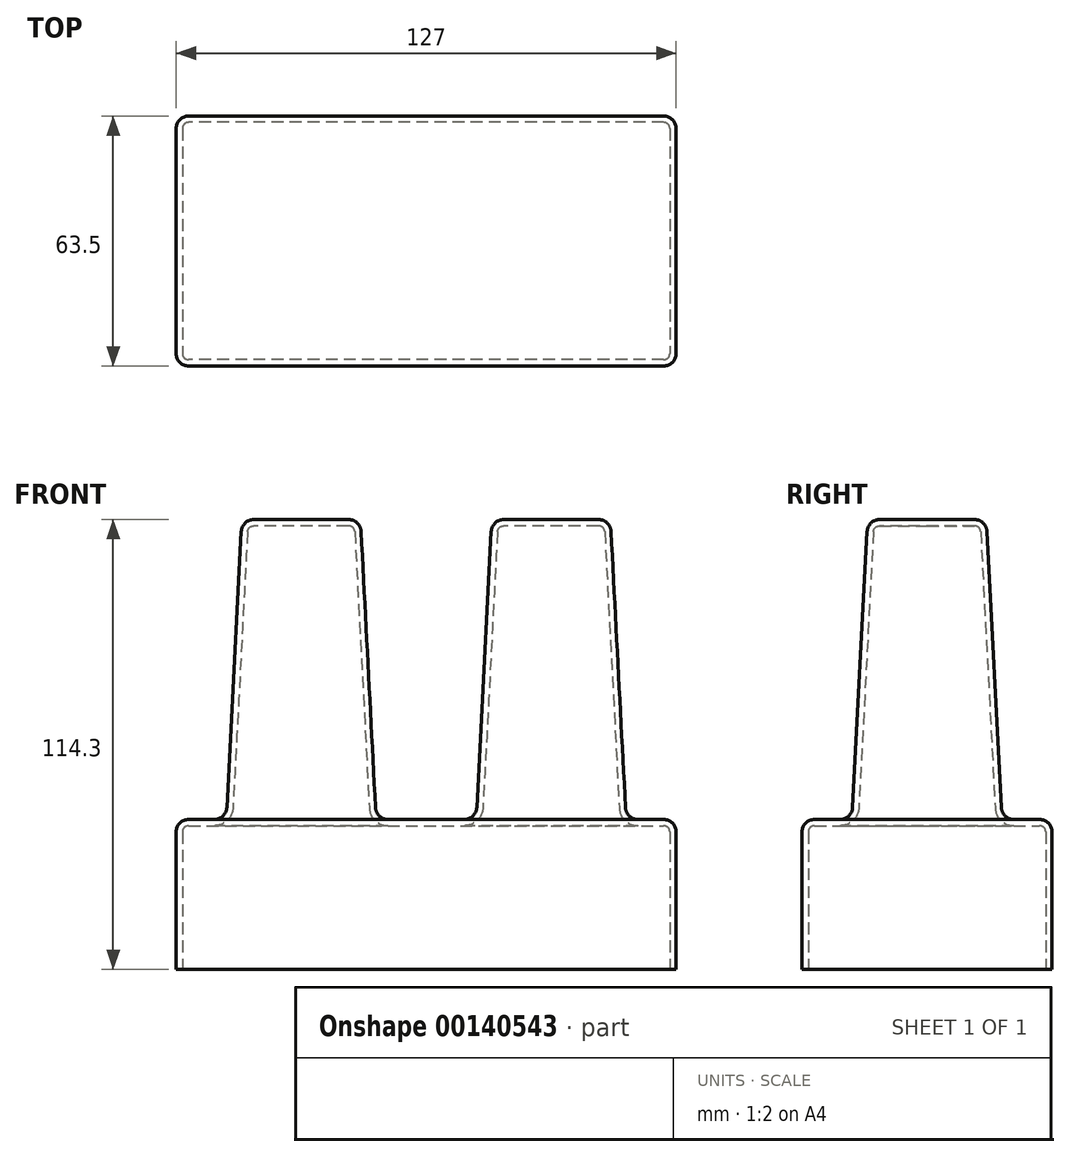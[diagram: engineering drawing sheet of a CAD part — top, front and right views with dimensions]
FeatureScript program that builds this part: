
annotation { "Feature Type Name" : "Feature", "Feature Type Description" : "" }
export const myFeature = defineFeature(function(context is Context, id is Id, definition is map)
    precondition{}
    {
        {
            var Q0;
            Q0=qCreatedBy(makeId("Top.planeOp"),FACE);
            var sketch = newSketch(context, id + "F0", { "sketchPlane" : qUnion([Q0])});
            skLineSegment(sketch, "E0.bottom", {"start": v(63.5, 31.75) * mm, "end": v(-63.5, 31.75) * mm});
            skLineSegment(sketch, "E0.top", {"start": v(63.5, -31.75) * mm, "end": v(-63.5, -31.75) * mm});
            skLineSegment(sketch, "E0.left", {"start": v(63.5, 31.75) * mm, "end": v(63.5, -31.75) * mm});
            skLineSegment(sketch, "E0.right", {"start": v(-63.5, 31.75) * mm, "end": v(-63.5, -31.75) * mm});
            skPoint(sketch, "E0.middle", {"position": v(0, 0) * mm});
            skSolve(sketch);
        }
        {
            var Q0;
            Q0 = qSketchRegion(id + "F0", true);
            extrude(context, id + "F1", {"entities" : qUnion([Q0]), "depth" : 38.1 * mm});
        }
        {
            var Q0;
            Q0=makeQuery(id+"F1.opExtrude","CAP_FACE",FACE,{"disambiguationData":[OSD([sQuery(id+"F0.wireOp",EDGE,"E0.bottom"),sQuery(id+"F0.wireOp",EDGE,"E0.top"),sQuery(id+"F0.wireOp",EDGE,"E0.left"),sQuery(id+"F0.wireOp",EDGE,"E0.right")])],"isStart":false});
            var sketch = newSketch(context, id + "F5", { "sketchPlane" : qUnion([Q0])});
            skCircle(sketch, "E1", {"center": v(-31.75, 0) * mm, "radius": 19.05 * mm});
            skCircle(sketch, "E2", {"center": v(31.75, 0) * mm, "radius": 19.05 * mm});
            skSolve(sketch);
        }
        {
            var Q0;
            Q0 = qSketchRegion(id + "F5", true);
            extrude(context, id + "F2", {"entities" : qUnion([Q0]), "operationType" : NewBodyOperationType.ADD, "depth" : 76.2 * mm, "hasDraft" : true, "draftAngle" : 3 * degree, "draftPullDirection" : true});
        }
        {
            var Q0;
            Q0=makeQuery(id+"F2.opExtrude","SWEPT_FACE",FACE,{"disambiguationData":[OSD([sQuery(id+"F5.wireOp",EDGE,"E2")])]});
            var Q1;
            Q1=makeQuery(id+"F2.opExtrude","SWEPT_FACE",FACE,{"disambiguationData":[OSD([sQuery(id+"F5.wireOp",EDGE,"E1")])]});
            var Q2;
            Q2=makeQuery(id+"F1.opExtrude","CAP_FACE",FACE,{"disambiguationData":[OSD([sQuery(id+"F0.wireOp",EDGE,"E0.bottom"),sQuery(id+"F0.wireOp",EDGE,"E0.top"),sQuery(id+"F0.wireOp",EDGE,"E0.left"),sQuery(id+"F0.wireOp",EDGE,"E0.right")])],"isStart":false});
            var Q3;
            Q3=makeQuery(id+"F1.opExtrude","SWEPT_EDGE",EDGE,{"disambiguationData":[OSD([sQuery(id+"F0.wireOp",EDGE,"E0.top"),sQuery(id+"F0.wireOp",EDGE,"E0.right")])]});
            var Q4;
            Q4=makeQuery(id+"F1.opExtrude","SWEPT_EDGE",EDGE,{"disambiguationData":[OSD([sQuery(id+"F0.wireOp",EDGE,"E0.bottom"),sQuery(id+"F0.wireOp",EDGE,"E0.right")])]});
            var Q5;
            Q5=makeQuery(id+"F1.opExtrude","SWEPT_EDGE",EDGE,{"disambiguationData":[OSD([sQuery(id+"F0.wireOp",EDGE,"E0.bottom"),sQuery(id+"F0.wireOp",EDGE,"E0.left")])]});
            var Q6;
            Q6=makeQuery(id+"F1.opExtrude","SWEPT_EDGE",EDGE,{"disambiguationData":[OSD([sQuery(id+"F0.wireOp",EDGE,"E0.top"),sQuery(id+"F0.wireOp",EDGE,"E0.left")])]});
            fillet(context, id + "F3", {"entities" : qUnion([Q0, Q1, Q2, Q3, Q4, Q5, Q6]), "radius" : 3.17 * mm, "tangentPropagation" : true, "allowEdgeOverflow" : false});
        }
        {
            var Q0;
            Q0=makeQuery(id+"F1.opExtrude","CAP_FACE",FACE,{"disambiguationData":[OSD([sQuery(id+"F0.wireOp",EDGE,"E0.bottom"),sQuery(id+"F0.wireOp",EDGE,"E0.top"),sQuery(id+"F0.wireOp",EDGE,"E0.left"),sQuery(id+"F0.wireOp",EDGE,"E0.right")])],"isStart":true});
            shell(context, id + "F4", {"entities" : qUnion([Q0]), "thickness" : 1.59 * mm});
        }
    });
